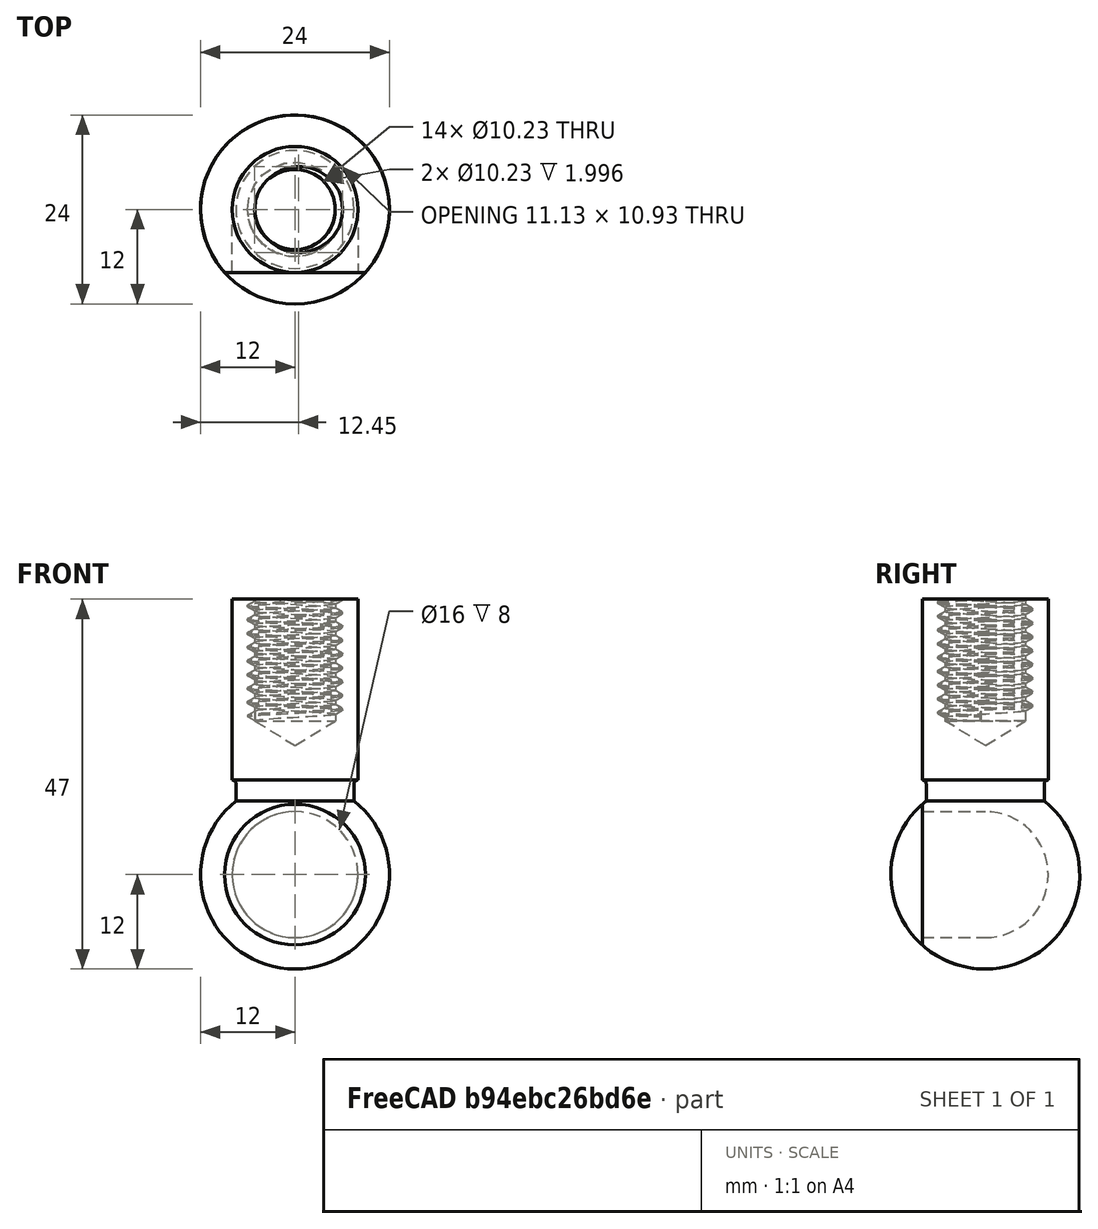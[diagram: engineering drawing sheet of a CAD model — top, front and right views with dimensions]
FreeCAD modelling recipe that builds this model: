
FCSTD DOCUMENT  (FreeCAD 1.0R39109 (Git))
Label: 3
License: All rights reserved
LicenseURL: https://en.wikipedia.org/wiki/All_rights_reserved
objects: PartDesign::AdditiveCylinder×2, Part::FeaturePython×2, PartDesign::AdditiveSphere×1, PartDesign::Hole×1, PartDesign::Fillet×1, PartDesign::Plane×1, PartDesign::Body×1, App::DocumentObjectGroup×1, Part::Sphere×1, Part::Cylinder×1, Part::MultiFuse×1, Part::Cut×1
note: 23 computed .brp shape members not serialized (recipe doc carries the construction recipe); baked Part::Feature solids carry a one-line shape summary decoded from their .brp

FEATURE [PartDesign::AdditiveSphere] Sphere
  Angle1 = -90
  Angle2 = 90
  Angle3 = 360
  AttacherType = Attacher::AttachEngine3D
  Radius = 12
  Refine = true
  Suppressed = false
FEATURE [PartDesign::AdditiveCylinder] Cylinder
  Angle = 360
  AttacherType = Attacher::AttachEngine3D
  BaseFeature = -> Sphere
  FirstAngle = 0
  Height = 35
  MapMode = 2
  Radius = 7.5
  Refine = true
  SecondAngle = 0
  Suppressed = false
FEATURE [PartDesign::AdditiveCylinder] Cylinder001
  Angle = 360
  AttacherType = Attacher::AttachEngine3D
  AttachmentOffset = pos=(0,0,-35) rot=(0,0,1;3.14159rad)
  AttachmentSupport = -> [XY_Plane]
  BaseFeature = -> Cylinder
  FirstAngle = 0
  Height = 23
  MapMode = 5
  Placement = pos=(0,0,35) rot=(1,0,0;3.14159rad)
  Radius = 8
  Refine = true
  SecondAngle = 0
  Suppressed = false
FEATURE [PartDesign::Hole] Hole
  BaseFeature = -> Cylinder001
  CustomThreadClearance = 0
  Depth = 15.5
  DepthType = 0
  Diameter = 10.234
  DrillForDepth = false
  DrillPoint = 1
  DrillPointAngle = 118
  HoleCutCountersinkAngle = 90
  HoleCutCustomValues = false
  HoleCutDepth = 0
  HoleCutDiameter = 0
  HoleCutType = 0
  ModelThread = true
  Placement = pos=(0,0,35) rot=(1,0,0;3.14159rad)
  Profile = -> Cylinder001 [Face5]
  Refine = true
  Suppressed = false
  Tapered = false
  TaperedAngle = 90
  ThreadClass = 0
  ThreadDepth = 15.5
  ThreadDepthType = 0
  ThreadDirection = 0
  ThreadFit = 0
  ThreadSize = 20
  ThreadType = 1
  Threaded = true
  UseCustomThreadClearance = false
FEATURE [PartDesign::Fillet] Fillet
  Base = -> Hole [Edge5]
  BaseFeature = -> Hole
  Placement = pos=(0,0,35) rot=(1,0,0;3.14159rad)
  Radius = 0.45
  Refine = true
  SupportTransform = false
  Suppressed = false
  UseAllEdges = false
FEATURE [PartDesign::Plane] DatumPlane
  AttachmentOffset = pos=(0,0,8) rot=(0,0,1;0rad)
  AttachmentSupport = -> [XZ_Plane]
  Length = 60.9545
  MapMode = 5
  Placement = pos=(0,-8,1.8e-15) rot=(1,0,0;1.5708rad)
  ResizeMode = 0
  Width = 70.9545
FEATURE [PartDesign::Body] Body
  AllowCompound = false
  Group = -> [Sphere,Cylinder,Cylinder001,Hole,Fillet,DatumPlane]
  Origin = -> Origin
  Tip = -> Fillet
FEATURE [Part::FeaturePython] Slice  # WARN: FeaturePython — macro-defined, semantics opaque (R4)
  Base = -> Fillet
  Mode = 1
  Tolerance = 0
  Tools = -> [DatumPlane]
FEATURE [App::DocumentObjectGroup] GrExplode_Slice  label="Exploded Slice"
FEATURE [Part::FeaturePython] Slice_child0  label="Slice.0"  # WARN: FeaturePython — macro-defined, semantics opaque (R4)
  Base = -> Slice
  FilterType = 1
  Invert = false
  OverrideMaxVal = 0
  WindowFrom = 80
  WindowTo = 100
  items = 0
FEATURE [Part::Sphere] Sphere001  label="Сфера"
  Angle1 = -90
  Angle2 = 90
  Angle3 = 360
  AttacherType = Attacher::AttachEngine3D
  Radius = 8
FEATURE [Part::Cylinder] Cylinder002  label="Цилиндр"
  Angle = 360
  AttacherType = Attacher::AttachEngine3D
  FirstAngle = 0
  Height = 12
  Placement = pos=(0,0,0) rot=(1,0,0;1.5708rad)
  Radius = 8
  SecondAngle = 0
FEATURE [Part::MultiFuse] Fusion
  Refine = true
  Shapes = -> [Sphere001,Cylinder002]
FEATURE [Part::Cut] Cut
  Base = -> Slice_child0
  Refine = true
  Tool = -> Fusion
